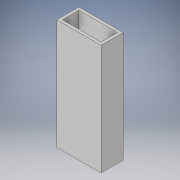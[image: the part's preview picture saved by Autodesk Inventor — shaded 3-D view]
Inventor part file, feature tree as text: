
AUTODESK INVENTOR PART (.ipt)
format: ipt  version: 2018 (Build 220112000, 112)  size: 98,304 bytes
history: native  units: in
note: dims shown in document units (in); Inventor stores cm internally (conversion verified against a paired STEP export)
features: extrude x1, sketch x1
ambient origin geometry x8: Origin, YZ Plane, XZ Plane, XY Plane, X Axis, Y Axis, Z Axis, Center Point
bodies: Solid1 (feature_tree)
feature tree (2):
  extrude  "Extrusion1"  Depth=1.0in
  sketch  "Sketch1"  dims[d0=2.0in d1=1.0in d2=0.125in d3=0.125in d4=0.125in d5=0.125in d6=5.0in d7=0.0in]
